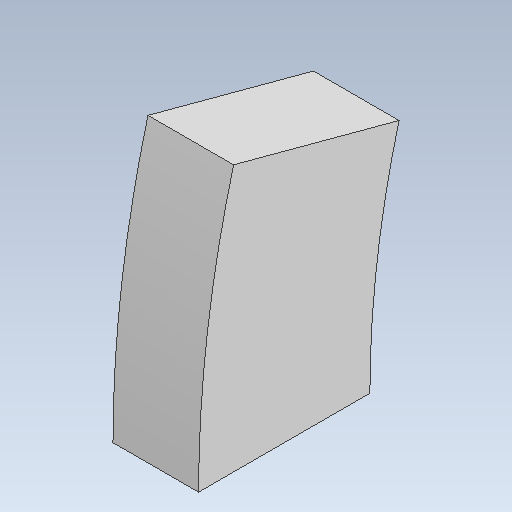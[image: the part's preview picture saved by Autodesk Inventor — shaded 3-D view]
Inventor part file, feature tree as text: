
AUTODESK INVENTOR PART (.ipt)
format: ipt  version: 2021 (Build 250183000, 183)  size: 106,496 bytes
history: native  units: mm
features: extrude x1
ambient origin geometry x8: Origin, YZ Plane, XZ Plane, XY Plane, X Axis, Y Axis, Z Axis, Center Point
bodies: Solid1 (feature_tree)
feature tree (1):
  extrude  "Extrusion1"  Depth=300.0mm
